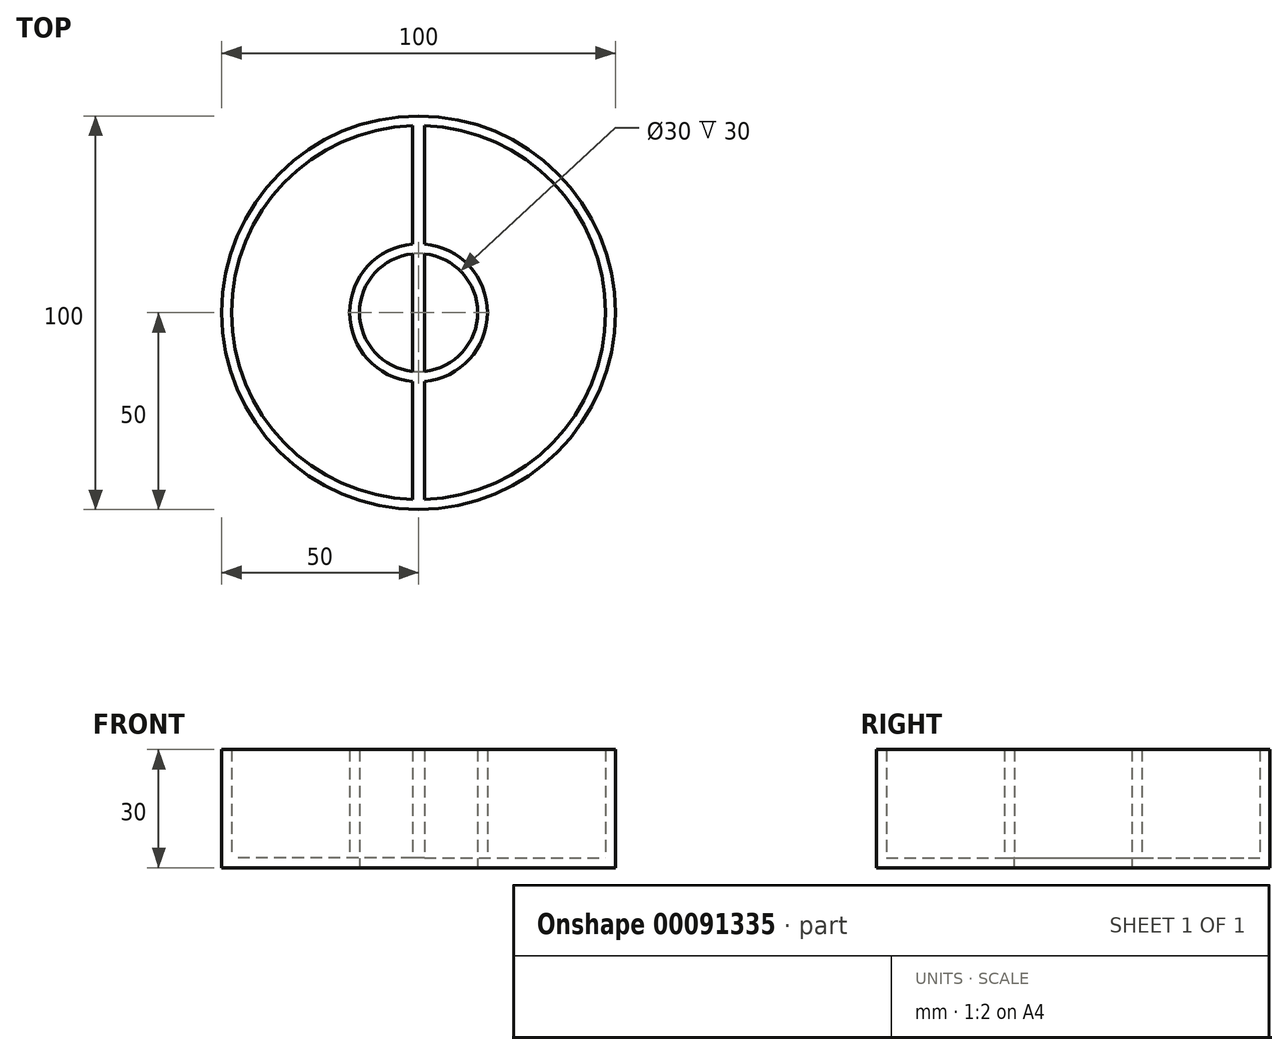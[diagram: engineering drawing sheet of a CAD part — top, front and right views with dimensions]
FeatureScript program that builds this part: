
annotation { "Feature Type Name" : "Feature", "Feature Type Description" : "" }
export const myFeature = defineFeature(function(context is Context, id is Id, definition is map)
    precondition{}
    {
        {
            var Q0;
            Q0=qCreatedBy(makeId("Top.planeOp"),FACE);
            var sketch = newSketch(context, id + "F0", { "sketchPlane" : qUnion([Q0])});
            skCircle(sketch, "E0", {"center": v(0, 0) * mm, "radius": 50 * mm});
            skCircle(sketch, "E1", {"center": v(0, 0) * mm, "radius": 15 * mm});
            skSolve(sketch);
        }
        {
            var Q0;
            Q0 = qSketchRegion(id + "F0", true);
            extrude(context, id + "F4", {"entities" : qUnion([Q0]), "depth" : 30 * mm});
        }
        {
            var Q0;
            Q0=makeQuery(id+"F4.opExtrude","CAP_FACE",FACE,{"disambiguationData":[OSD([sQuery(id+"F0.wireOp",EDGE,"E0"),sQuery(id+"F0.wireOp",EDGE,"E1")])],"isStart":false});
            shell(context, id + "F1", {"entities" : qUnion([Q0]), "thickness" : 2.5 * mm});
        }
        {
            var Q0;
            {var subQ0=sQuery(id+"F0.wireOp",EDGE,"E1");var subQ1=sQuery(id+"F0.wireOp",EDGE,"E0");Q0=makeQuery(id+"F1.opShell","OFFSET_FACE",FACE,{"disambiguationData":[OSD([subQ1,subQ0]),TDD([makeQuery(id+"F4.opExtrude","CAP_FACE",FACE,{"disambiguationData":[OSD([subQ1,subQ0])],"isStart":true})])]});}
            var sketch = newSketch(context, id + "F2", { "sketchPlane" : qUnion([Q0])});
            skLineSegment(sketch, "E2.bottom", {"start": v(1.5, -49.98) * mm, "end": v(-1.5, -49.98) * mm});
            skLineSegment(sketch, "E2.top", {"start": v(1.5, 49.98) * mm, "end": v(-1.5, 49.98) * mm});
            skLineSegment(sketch, "E2.left", {"start": v(1.5, -49.98) * mm, "end": v(1.5, 49.98) * mm});
            skLineSegment(sketch, "E2.right", {"start": v(-1.5, -49.98) * mm, "end": v(-1.5, 49.98) * mm});
            skPoint(sketch, "E2.middle", {"position": v(0, 0) * mm});
            skSolve(sketch);
        }
        {
            var Q0;
            Q0 = qSketchRegion(id + "F2", true);
            extrude(context, id + "F5", {"entities" : qUnion([Q0]), "operationType" : NewBodyOperationType.ADD, "depth" : 27.5 * mm});
        }
    });
